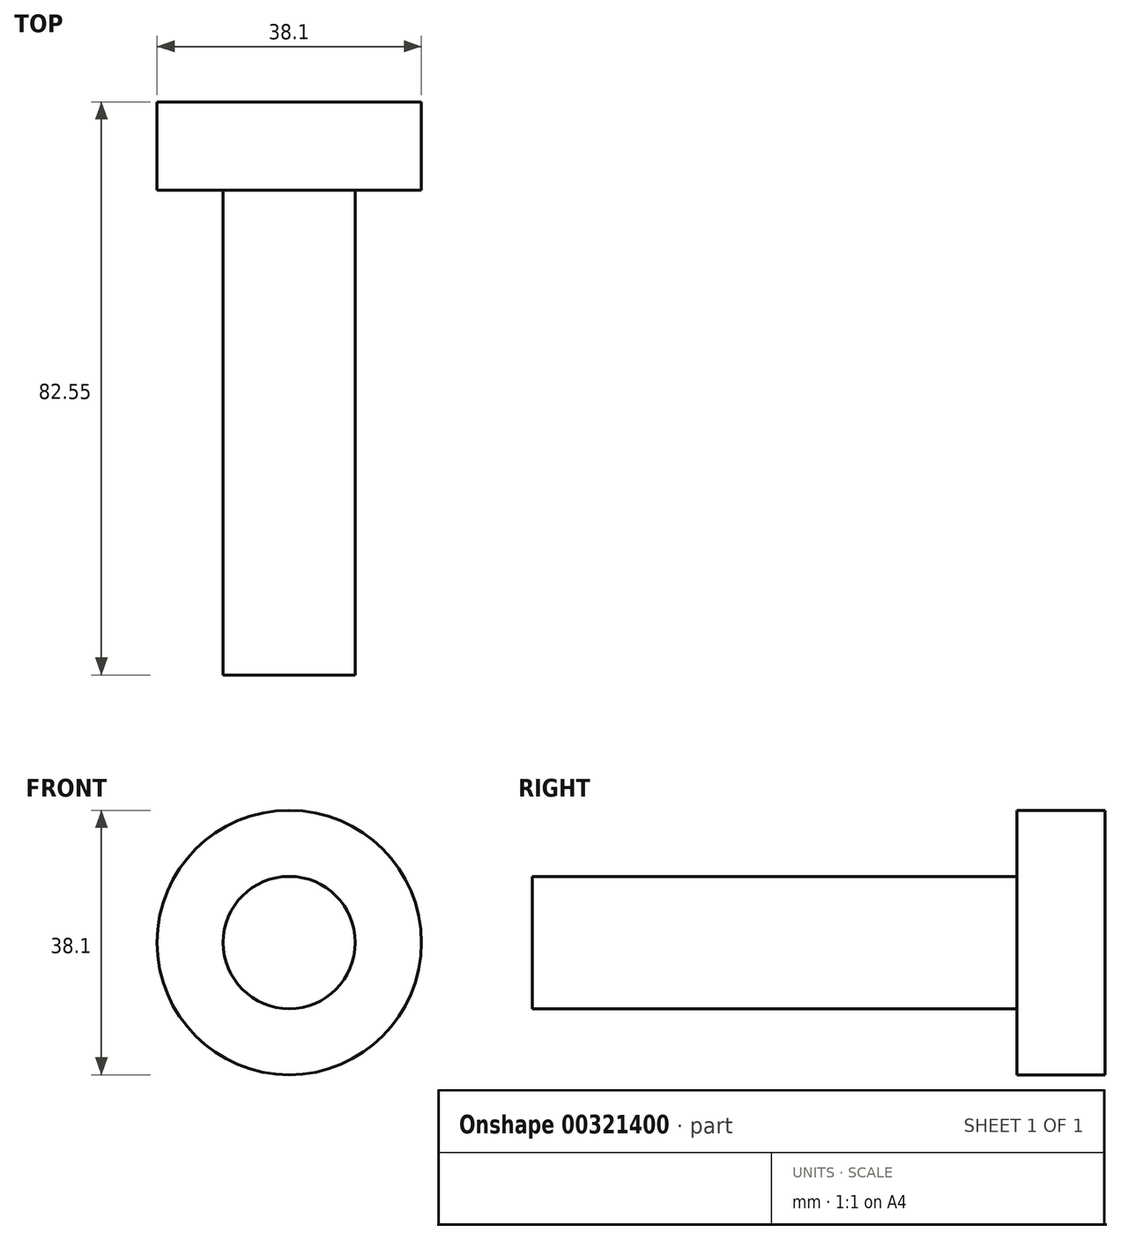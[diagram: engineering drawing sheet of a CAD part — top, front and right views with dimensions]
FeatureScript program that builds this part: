
annotation { "Feature Type Name" : "Feature", "Feature Type Description" : "" }
export const myFeature = defineFeature(function(context is Context, id is Id, definition is map)
    precondition{}
    {
        {
            var Q0;
            Q0=qCreatedBy(makeId("Front.planeOp"),FACE);
            var sketch = newSketch(context, id + "F0", { "sketchPlane" : qUnion([Q0])});
            skCircle(sketch, "E0", {"center": v(0, 0) * mm, "radius": 19.05 * mm});
            skSolve(sketch);
        }
        {
            var Q0;
            Q0=qCreatedBy(makeId("Front.planeOp"),FACE);
            var sketch = newSketch(context, id + "F1", { "sketchPlane" : qUnion([Q0])});
            skCircle(sketch, "E1", {"center": v(0, 0) * mm, "radius": 9.53 * mm});
            skSolve(sketch);
        }
        {
            var Q0;
            Q0 = qSketchRegion(id + "F0", true);
            extrude(context, id + "F2", {"entities" : qUnion([Q0]), "endBound" : BoundingType.SYMMETRIC, "depth" : 12.7 * mm});
        }
        {
            var Q0;
            Q0 = qSketchRegion(id + "F1", true);
            extrude(context, id + "F3", {"entities" : qUnion([Q0]), "operationType" : NewBodyOperationType.ADD, "depth" : 76.2 * mm});
        }
    });
